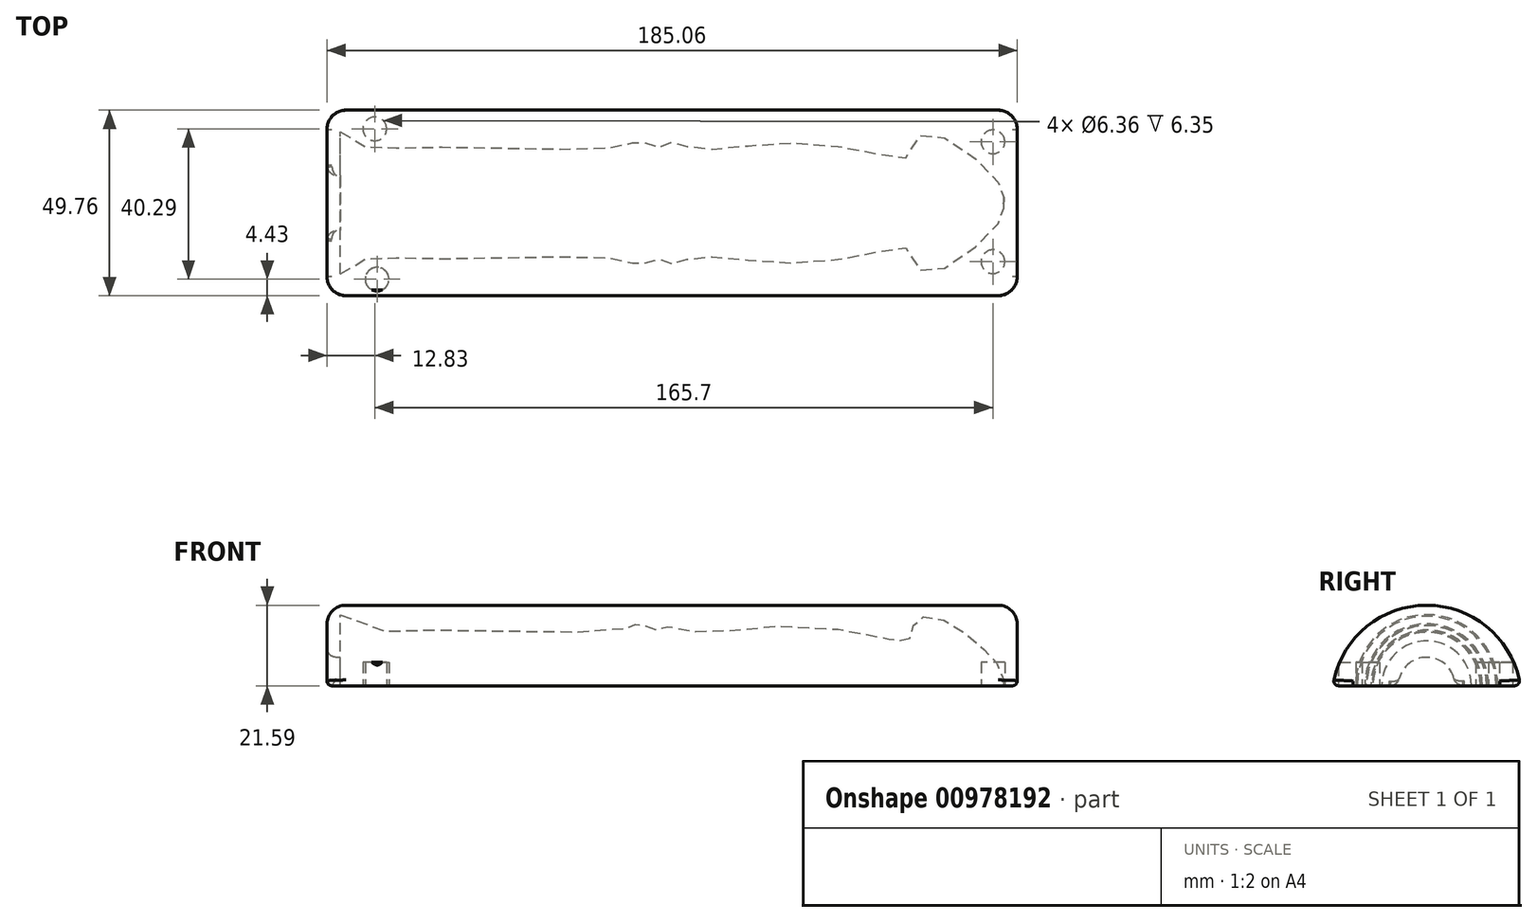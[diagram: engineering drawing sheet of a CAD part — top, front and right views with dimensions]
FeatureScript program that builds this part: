
annotation { "Feature Type Name" : "Feature", "Feature Type Description" : "" }
export const myFeature = defineFeature(function(context is Context, id is Id, definition is map)
    precondition{}
    {
        {
            var Q0;
            Q0=qCreatedBy(makeId("Front.planeOp"),FACE);
            var sketch = newSketch(context, id + "F0", { "sketchPlane" : qUnion([Q0])});
            skLineSegment(sketch, "E0.right", {"start": v(-88.9, 19.05) * mm, "end": v(-88.9, 0) * mm});
            skPoint(sketch, "E0.middle", {"position": v(0, 0) * mm});
            skLineSegment(sketch, "E1", {"start": v(-88.9, 0) * mm, "end": v(88.9, 0) * mm});
            skFitSpline(sketch, "E2", {"points": [v(-88.9, 19.05) * mm, v(-68.88, 14.9) * mm, v(-12.62, 15.36) * mm, v(-8.8, 16.59) * mm, v(-3.86, 14.96) * mm, v(0, 16.28) * mm, v(6.03, 14.62) * mm, v(37.07, 15.98) * mm, v(63.33, 12.23) * mm, v(64, 14.28) * mm, v(68.77, 18.66) * mm, v(87.5, 5.49) * mm, v(88.9, 0) * mm], "startDerivative": vector(153.99, -157.05) * mm, "endDerivative": vector(-4.41, -120.62) * mm});
            skSolve(sketch);
        }
        {
            var Q0;
            Q0=makeQuery(id+"F0.imprint","IMPRINT",FACE,{"disambiguationData":[TD([[makeQuery(id+"F0.imprint","IMPRINT",EDGE,{"derivedFrom":sQuery(id+"F0.wireOp",EDGE,"E0.right")}),1.0]])]});
            var Q1;
            Q1=sQuery(id+"F0.wireOp",EDGE,"E1");
            revolve(context, id + "F1", {"surfaceOperationType" : NewSurfaceOperationType.NEW, "entities" : qUnion([Q0]), "axis" : qUnion([Q1]), "revolveType" : RevolveType.FULL});
        }
        {
            var Q0;
            Q0=qCreatedBy(makeId("Top.planeOp"),FACE);
            var sketch = newSketch(context, id + "F2", { "sketchPlane" : qUnion([Q0])});
            skLineSegment(sketch, "E3.bottom", {"start": v(89.99, 25.13) * mm, "end": v(-89.99, 25.13) * mm});
            skLineSegment(sketch, "E3.top", {"start": v(89.99, -25.13) * mm, "end": v(-89.99, -25.13) * mm});
            skLineSegment(sketch, "E3.left", {"start": v(92.53, 22.59) * mm, "end": v(92.53, -22.59) * mm});
            skLineSegment(sketch, "E3.right", {"start": v(-92.53, 22.59) * mm, "end": v(-92.53, -22.59) * mm});
            skPoint(sketch, "E3.middle", {"position": v(0, 0) * mm});
            skPoint(sketch, "E4.visualSharp", {"position": v(-92.53, 25.13) * mm});
            skArc(sketch, "E4.filletArc", {"start": v(-89.99, 25.13) * mm, "mid": v(-91.78, 24.38) * mm, "end": v(-92.53, 22.59) * mm});
            skPoint(sketch, "E5.visualSharp", {"position": v(-92.53, -25.13) * mm});
            skArc(sketch, "E5.filletArc", {"start": v(-92.53, -22.59) * mm, "mid": v(-91.78, -24.38) * mm, "end": v(-89.99, -25.13) * mm});
            skPoint(sketch, "E6.visualSharp", {"position": v(92.53, 25.13) * mm});
            skArc(sketch, "E6.filletArc", {"start": v(92.53, 22.59) * mm, "mid": v(91.78, 24.38) * mm, "end": v(89.99, 25.13) * mm});
            skPoint(sketch, "E7.visualSharp", {"position": v(92.53, -25.13) * mm});
            skArc(sketch, "E7.filletArc", {"start": v(89.99, -25.13) * mm, "mid": v(91.78, -24.38) * mm, "end": v(92.53, -22.59) * mm});
            skCircle(sketch, "E8", {"center": v(86, 16.37) * mm, "radius": 3.18 * mm});
            skCircle(sketch, "E9", {"center": v(86, -15.77) * mm, "radius": 3.18 * mm});
            skCircle(sketch, "E10", {"center": v(-79.7, 19.84) * mm, "radius": 3.18 * mm});
            skCircle(sketch, "E11", {"center": v(-79.1, -20.45) * mm, "radius": 3.18 * mm});
            skSolve(sketch);
        }
        {
            var Q0;
            Q0=makeQuery(id+"F2.imprint","IMPRINT",FACE,{"disambiguationData":[TD([[makeQuery(id+"F2.imprint","IMPRINT",EDGE,{"derivedFrom":sQuery(id+"F2.wireOp",EDGE,"E3.bottom")}),1.0]])]});
            var Q1;
            Q1=makeQuery(id+"F2.imprint","IMPRINT",FACE,{"disambiguationData":[TD([[makeQuery(id+"F2.imprint","IMPRINT",EDGE,{"derivedFrom":sQuery(id+"F2.wireOp",EDGE,"E8")}),1.0]])]});
            var Q2;
            Q2=makeQuery(id+"F2.imprint","IMPRINT",FACE,{"disambiguationData":[TD([[makeQuery(id+"F2.imprint","IMPRINT",EDGE,{"derivedFrom":sQuery(id+"F2.wireOp",EDGE,"E9")}),1.0]])]});
            var Q3;
            Q3=makeQuery(id+"F2.imprint","IMPRINT",FACE,{"disambiguationData":[TD([[makeQuery(id+"F2.imprint","IMPRINT",EDGE,{"derivedFrom":sQuery(id+"F2.wireOp",EDGE,"E11")}),1.0]])]});
            var Q4;
            Q4=makeQuery(id+"F2.imprint","IMPRINT",FACE,{"disambiguationData":[TD([[makeQuery(id+"F2.imprint","IMPRINT",EDGE,{"derivedFrom":sQuery(id+"F2.wireOp",EDGE,"E10")}),1.0]])]});
            extrude(context, id + "F3", {"entities" : qUnion([Q0, Q1, Q2, Q3, Q4]), "depth" : 21.59 * mm, "offsetDistance" : 25.4 * mm});
        }
        {
            var Q0;
            Q0=makeQuery(id+"F1.opRevolve","SWEPT_BODY",BODY,{"disambiguationData":[OSD([sQuery(id+"F0.wireOp",EDGE,"E0.right"),sQuery(id+"F0.wireOp",EDGE,"E1"),sQuery(id+"F0.wireOp",EDGE,"E2")])]});
            var Q1;
            Q1=makeQuery(id+"F3.opExtrude","SWEPT_BODY",BODY,{"disambiguationData":[OSD([sQuery(id+"F2.wireOp",EDGE,"E3.bottom"),sQuery(id+"F2.wireOp",EDGE,"E3.top"),sQuery(id+"F2.wireOp",EDGE,"E3.left"),sQuery(id+"F2.wireOp",EDGE,"E3.right"),sQuery(id+"F2.wireOp",EDGE,"E4.filletArc"),sQuery(id+"F2.wireOp",EDGE,"E5.filletArc"),sQuery(id+"F2.wireOp",EDGE,"E6.filletArc"),sQuery(id+"F2.wireOp",EDGE,"E7.filletArc")])]});
            booleanBodies(context, id + "F4", {"operationType" : BooleanOperationType.SUBTRACTION, "tools" : qUnion([Q0]), "targets" : qUnion([Q1])});
        }
        {
            var Q0;
            Q0=makeQuery(id+"F3.opExtrude","CAP_EDGE",EDGE,{"disambiguationData":[OSD([sQuery(id+"F2.wireOp",EDGE,"E3.top")])],"isStart":false});
            var Q1;
            Q1=makeQuery(id+"F3.opExtrude","CAP_EDGE",EDGE,{"disambiguationData":[OSD([sQuery(id+"F2.wireOp",EDGE,"E3.bottom")])],"isStart":false});
            fillet(context, id + "F5", {"entities" : qUnion([Q0, Q1]), "radius" : 25.4 * mm, "allowEdgeOverflow" : false});
        }
        {
            var Q0;
            Q0=makeQuery(id+"F5.opFillet","BLEND_EDGE",EDGE,{"blendedFrom":[makeQuery(id+"F3.opExtrude","CAP_EDGE",EDGE,{"disambiguationData":[OSD([sQuery(id+"F2.wireOp",EDGE,"E3.bottom")])],"isStart":false}),makeQuery(id+"F3.opExtrude","SWEPT_FACE",FACE,{"disambiguationData":[OSD([sQuery(id+"F2.wireOp",EDGE,"E3.left")])]})],"blendedInto":[makeQuery(id+"F3.opExtrude","SWEPT_FACE",FACE,{"disambiguationData":[OSD([sQuery(id+"F2.wireOp",EDGE,"E3.left")])]})]});
            var Q1;
            Q1=makeQuery(id+"F5.opFillet","BLEND_EDGE",EDGE,{"blendedFrom":[makeQuery(id+"F3.opExtrude","CAP_EDGE",EDGE,{"disambiguationData":[OSD([sQuery(id+"F2.wireOp",EDGE,"E3.top")])],"isStart":false}),makeQuery(id+"F3.opExtrude","SWEPT_FACE",FACE,{"disambiguationData":[OSD([sQuery(id+"F2.wireOp",EDGE,"E3.right")])]})],"blendedInto":[makeQuery(id+"F3.opExtrude","SWEPT_FACE",FACE,{"disambiguationData":[OSD([sQuery(id+"F2.wireOp",EDGE,"E3.right")])]})]});
            fillet(context, id + "F6", {"entities" : qUnion([Q0, Q1]), "radius" : 5.08 * mm, "tangentPropagation" : true, "allowEdgeOverflow" : false});
        }
        {
            var Q0;
            {var subQ0=sQuery(id+"F2.wireOp",EDGE,"E3.top");Q0=makeQuery(id+"F5.opFillet","BLEND_EDGE",EDGE,{"blendedFrom":[makeQuery(id+"F3.opExtrude","CAP_EDGE",EDGE,{"disambiguationData":[OSD([subQ0])],"isStart":false}),makeQuery(id+"F3.opExtrude","CAP_FACE",FACE,{"disambiguationData":[OSD([sQuery(id+"F2.wireOp",EDGE,"E3.bottom"),subQ0,sQuery(id+"F2.wireOp",EDGE,"E3.left"),sQuery(id+"F2.wireOp",EDGE,"E3.right"),sQuery(id+"F2.wireOp",EDGE,"E4.filletArc"),sQuery(id+"F2.wireOp",EDGE,"E5.filletArc"),sQuery(id+"F2.wireOp",EDGE,"E6.filletArc"),sQuery(id+"F2.wireOp",EDGE,"E7.filletArc")])],"isStart":true})],"blendedInto":[makeQuery(id+"F3.opExtrude","CAP_FACE",FACE,{"disambiguationData":[OSD([sQuery(id+"F2.wireOp",EDGE,"E3.bottom"),subQ0,sQuery(id+"F2.wireOp",EDGE,"E3.left"),sQuery(id+"F2.wireOp",EDGE,"E3.right"),sQuery(id+"F2.wireOp",EDGE,"E4.filletArc"),sQuery(id+"F2.wireOp",EDGE,"E5.filletArc"),sQuery(id+"F2.wireOp",EDGE,"E6.filletArc"),sQuery(id+"F2.wireOp",EDGE,"E7.filletArc")])],"isStart":true})]});}
            fillet(context, id + "F7", {"entities" : qUnion([Q0]), "radius" : 1.27 * mm, "tangentPropagation" : true, "allowEdgeOverflow" : false});
        }
        {
            var Q0;
            Q0=qCreatedBy(makeId("Top.planeOp"),FACE);
            var sketch = newSketch(context, id + "F8", { "sketchPlane" : qUnion([Q0])});
            skLineSegment(sketch, "E12", {"start": v(-96.64, 0) * mm, "end": v(55.98, 0) * mm});
            skLineSegment(sketch, "E13", {"start": v(55.98, 0) * mm, "end": v(55.98, 7.62) * mm});
            skLineSegment(sketch, "E14", {"start": v(55.98, 7.62) * mm, "end": v(-96.64, 7.62) * mm});
            skLineSegment(sketch, "E15", {"start": v(-96.64, 7.62) * mm, "end": v(-96.64, 0) * mm});
            skSolve(sketch);
        }
        {
            var Q0;
            Q0=makeQuery(id+"F8.imprint","IMPRINT",FACE,{"disambiguationData":[TD([[makeQuery(id+"F8.imprint","IMPRINT",EDGE,{"derivedFrom":sQuery(id+"F8.wireOp",EDGE,"E12")}),1.0]])]});
            var Q1;
            Q1=sQuery(id+"F8.wireOp",EDGE,"E12");
            revolve(context, id + "F9", {"surfaceOperationType" : NewSurfaceOperationType.NEW, "entities" : qUnion([Q0]), "axis" : qUnion([Q1]), "revolveType" : RevolveType.FULL});
        }
        {
            var Q0;
            Q0=makeQuery(id+"F9.opRevolve","SWEPT_EDGE",EDGE,{"disambiguationData":[OSD([sQuery(id+"F8.wireOp",EDGE,"E13"),sQuery(id+"F8.wireOp",EDGE,"E14")])]});
            fillet(context, id + "F10", {"entities" : qUnion([Q0]), "radius" : 5.08 * mm, "tangentPropagation" : true, "allowEdgeOverflow" : false});
        }
        {
            var Q0;
            Q0=makeQuery(id+"F9.opRevolve","SWEPT_BODY",BODY,{"disambiguationData":[OSD([sQuery(id+"F8.wireOp",EDGE,"E12"),sQuery(id+"F8.wireOp",EDGE,"E13"),sQuery(id+"F8.wireOp",EDGE,"E14"),sQuery(id+"F8.wireOp",EDGE,"E15")])]});
            var Q1;
            Q1=makeQuery(id+"F3.opExtrude","SWEPT_BODY",BODY,{"disambiguationData":[OSD([sQuery(id+"F2.wireOp",EDGE,"E3.bottom"),sQuery(id+"F2.wireOp",EDGE,"E3.top"),sQuery(id+"F2.wireOp",EDGE,"E3.left"),sQuery(id+"F2.wireOp",EDGE,"E3.right"),sQuery(id+"F2.wireOp",EDGE,"E4.filletArc"),sQuery(id+"F2.wireOp",EDGE,"E5.filletArc"),sQuery(id+"F2.wireOp",EDGE,"E6.filletArc"),sQuery(id+"F2.wireOp",EDGE,"E7.filletArc")])]});
            booleanBodies(context, id + "F11", {"operationType" : BooleanOperationType.SUBTRACTION, "tools" : qUnion([Q0]), "targets" : qUnion([Q1])});
        }
        {
            var Q0;
            Q0=makeQuery(id+"F11.opBoolean","INTERSECT",EDGE,{"derivedFrom":[makeQuery(id+"F3.opExtrude","SWEPT_FACE",FACE,{"disambiguationData":[OSD([sQuery(id+"F2.wireOp",EDGE,"E3.right")])]}),makeQuery(id+"F9.opRevolve","SWEPT_FACE",FACE,{"disambiguationData":[OSD([sQuery(id+"F8.wireOp",EDGE,"E14")])]})]});
            fillet(context, id + "F12", {"entities" : qUnion([Q0]), "radius" : 2.54 * mm, "tangentPropagation" : true, "allowEdgeOverflow" : false});
        }
        {
            var Q0;
            Q0=makeQuery(id+"F2.imprint","IMPRINT",FACE,{"disambiguationData":[TD([[makeQuery(id+"F2.imprint","IMPRINT",EDGE,{"derivedFrom":sQuery(id+"F2.wireOp",EDGE,"E10")}),1.0]])]});
            var Q1;
            Q1=makeQuery(id+"F2.imprint","IMPRINT",FACE,{"disambiguationData":[TD([[makeQuery(id+"F2.imprint","IMPRINT",EDGE,{"derivedFrom":sQuery(id+"F2.wireOp",EDGE,"E11")}),1.0]])]});
            var Q2;
            Q2=makeQuery(id+"F2.imprint","IMPRINT",FACE,{"disambiguationData":[TD([[makeQuery(id+"F2.imprint","IMPRINT",EDGE,{"derivedFrom":sQuery(id+"F2.wireOp",EDGE,"E8")}),1.0]])]});
            var Q3;
            Q3=makeQuery(id+"F2.imprint","IMPRINT",FACE,{"disambiguationData":[TD([[makeQuery(id+"F2.imprint","IMPRINT",EDGE,{"derivedFrom":sQuery(id+"F2.wireOp",EDGE,"E9")}),1.0]])]});
            extrude(context, id + "F13", {"entities" : qUnion([Q0, Q1, Q2, Q3]), "operationType" : NewBodyOperationType.REMOVE, "depth" : 6.35 * mm, "offsetDistance" : 25.4 * mm});
        }
    });
